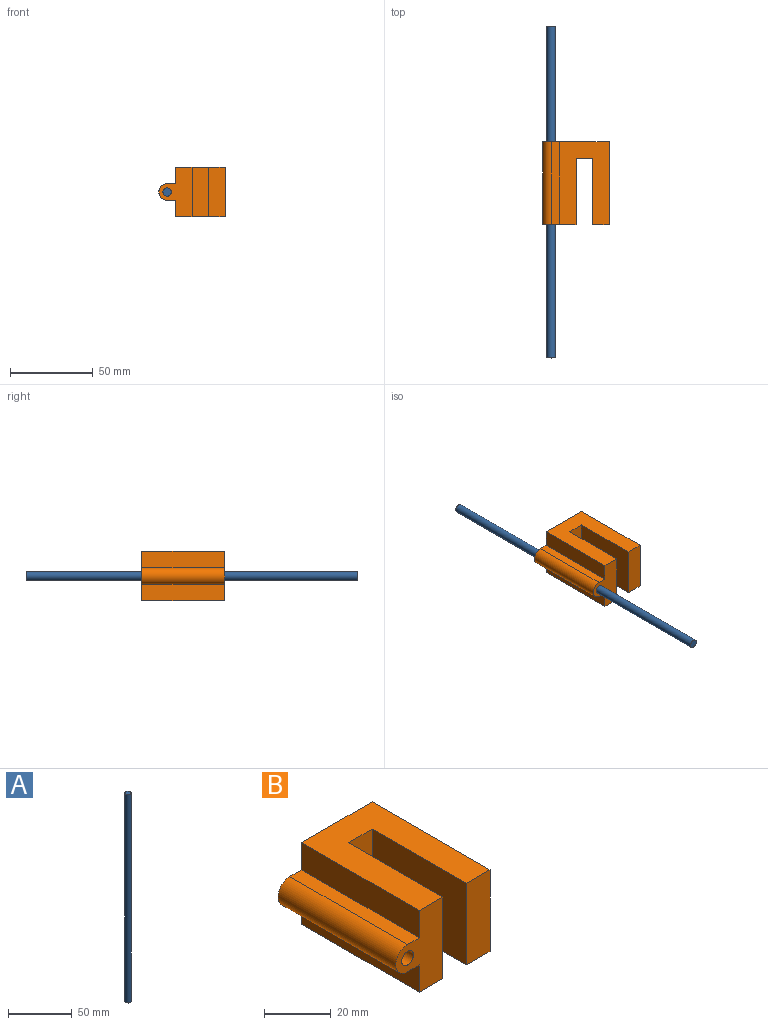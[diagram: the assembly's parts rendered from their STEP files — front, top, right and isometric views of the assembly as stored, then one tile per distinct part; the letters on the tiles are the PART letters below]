
ASSEMBLY  parts=2 mates=1
PART A: 3 faces, bbox 5x5x200 mm
  f0: cylinder r=2.5mm len=200mm, axis (0,0,-1), area 3141.6mm2, adj f1,f2
  f1: plane 5x5mm, normal (0,0,1), area 19.6mm2, adj f0
  f2: plane 5x5mm, normal (0,0,-1), area 19.6mm2, adj f0
PART B: 15 faces, bbox 40x50x30 mm
  f0: cylinder r=2.5mm len=50mm, axis (0,1,0), area 785.4mm2, adj f2,f3
  f1: cylinder r=5mm len=50mm, axis (0,1,0), area 785.4mm2, adj f2,f3,f4,f6
  f2: plane 30x20mm, normal (0,-1,0), area 369.6mm2, adj f0,f1,f4,f5,f6,f7,f8,f13
  f3: plane 40x30mm, normal (0,1,0), area 969.6mm2, adj f0,f1,f4,f5,f6,f7,f12,f13
  f4: plane 50x5mm, normal (0,0,-1), area 250mm2, adj f1,f2,f3,f5
  f5: plane 50x10mm, normal (-1,0,0), area 500mm2, adj f2,f3,f4,f14
  f6: plane 50x5mm, normal (0,0,1), area 250mm2, adj f1,f2,f3,f7
  f7: plane 50x10mm, normal (-1,0,0), area 500mm2, adj f2,f3,f6,f13
  f8: plane 40x30mm, normal (1,0,0), area 1200mm2, adj f2,f9,f13,f14
  f9: plane 30x10mm, normal (0,-1,0), area 300mm2, adj f8,f10,f13,f14
  f10: plane 40x30mm, normal (-1,0,0), area 1200mm2, adj f9,f11,f13,f14
  f11: plane 30x10mm, normal (0,-1,0), area 300mm2, adj f10,f12,f13,f14
  f12: plane 50x30mm, normal (1,0,0), area 1500mm2, adj f3,f11,f13,f14
  f13: plane 50x30mm, normal (0,0,1), area 1100mm2, adj f2,f3,f7,f8,f9,f10,f11,f12
  f14: plane 50x30mm, normal (0,0,-1), area 1100mm2, adj f2,f3,f5,f8,f9,f10,f11,f12
PLACE A rot(axis=(-0.98,-0.14,-0.14),91.2deg) t=(-14.31,-80.35,15)mm
PLACE B at identity fixed
MATE cylindrical A.f0 <-> B.f0  axis (0,-1,0) through (-14.31,-80.35,15)mm
